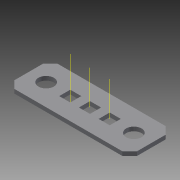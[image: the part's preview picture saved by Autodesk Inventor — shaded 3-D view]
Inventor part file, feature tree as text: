
AUTODESK INVENTOR PART (.ipt)
format: ipt  version: 2015 (Build 190159000, 159)  size: 118,784 bytes
history: native  units: in
note: dims shown in document units (in); Inventor stores cm internally (conversion verified against a paired STEP export)
features: other x6, pattern_linear x1, imported_body x1
ambient origin geometry x8: Origin, YZ Plane, XZ Plane, XY Plane, X Axis, Y Axis, Z Axis, Center Point
bodies: Body1 (feature_tree)
feature tree (8):
  other  "Bar Lock"
  parser-record x1  (decoder bookkeeping rows leaked as tree rows — omitted from the tree; the rows remain in map.json)
  other  "axis"
  pattern_linear  "axes"  Spacing1=0.0in  [1 undecoded]
  imported_body  "Base1"
  other  "Work Point1"
  other  "Work Axis2"
  other  "Work Axis3"
note: 1 required parameter value undecoded (feature->parameter linkage not recoverable at this tier; creation-order binding heuristic only, values carry confidence <= 0.55)
